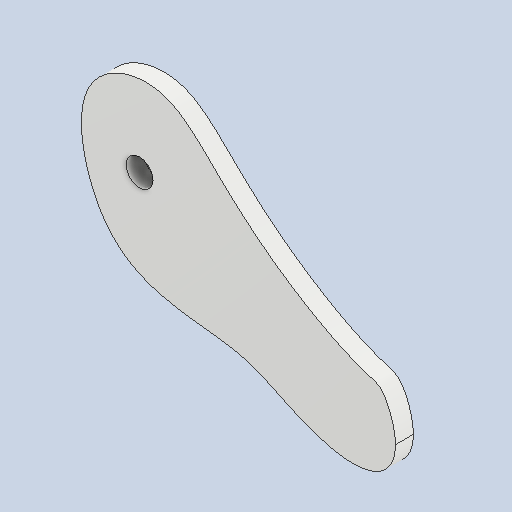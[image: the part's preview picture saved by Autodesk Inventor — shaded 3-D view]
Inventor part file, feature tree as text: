
AUTODESK INVENTOR PART (.ipt)
format: ipt  version: 2022 (Build 260153000, 153)  size: 104,960 bytes
history: native  units: in
note: dims shown in document units (in); Inventor stores cm internally (conversion verified against a paired STEP export)
features: other x3, sketch x1
ambient origin geometry x8: Origin, YZ Plane, XZ Plane, XY Plane, X Axis, Y Axis, Z Axis, Center Point
bodies: Solid1 (feature_tree)
feature tree (4):
  other  "Component34.ipt"
  other  "Solid1::Component34.ipt"
  other  "TaggingFeature1"
  sketch  "Sketch2"  dims[d0=0.3937in]
